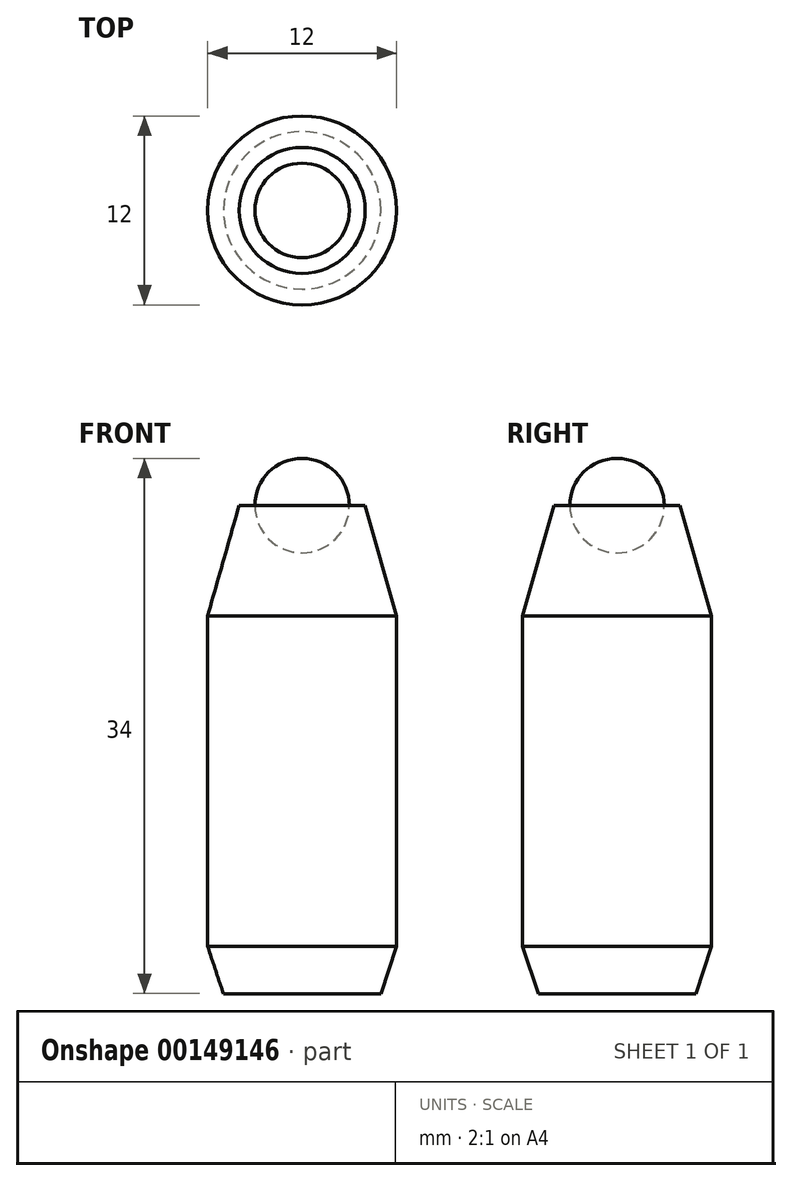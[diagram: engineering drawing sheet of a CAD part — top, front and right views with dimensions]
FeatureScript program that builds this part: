
annotation { "Feature Type Name" : "Feature", "Feature Type Description" : "" }
export const myFeature = defineFeature(function(context is Context, id is Id, definition is map)
    precondition{}
    {
        {
            var Q0;
            Q0=qCreatedBy(makeId("Front.planeOp"),FACE);
            var sketch = newSketch(context, id + "F0", { "sketchPlane" : qUnion([Q0])});
            skLineSegment(sketch, "E0", {"start": v(0, -13.95) * mm, "end": v(0, 17.05) * mm});
            skLineSegment(sketch, "E1", {"start": v(0, 17.05) * mm, "end": v(4, 17.05) * mm});
            skLineSegment(sketch, "E2", {"start": v(4, 17.05) * mm, "end": v(6, 10.05) * mm});
            skLineSegment(sketch, "E3", {"start": v(6, 10.05) * mm, "end": v(6, -10.95) * mm});
            skLineSegment(sketch, "E4", {"start": v(6, -10.95) * mm, "end": v(5, -13.95) * mm});
            skLineSegment(sketch, "E5", {"start": v(5, -13.95) * mm, "end": v(0, -13.95) * mm});
            skSolve(sketch);
        }
        {
            var Q0;
            Q0=makeQuery(id+"F0.imprint","IMPRINT",FACE,{"disambiguationData":[TD([[makeQuery(id+"F0.imprint","IMPRINT",EDGE,{"derivedFrom":sQuery(id+"F0.wireOp",EDGE,"E0")}),-1.0]])]});
            var Q1;
            Q1=sQuery(id+"F0.wireOp",EDGE,"E0");
            revolve(context, id + "F1", {"entities" : qUnion([Q0]), "axis" : qUnion([Q1]), "revolveType" : RevolveType.FULL});
        }
        {
            var Q0;
            Q0=makeQuery(id+"F1.opRevolve","SWEPT_FACE",FACE,{"disambiguationData":[OSD([sQuery(id+"F0.wireOp",EDGE,"E1")])]});
            var sketch = newSketch(context, id + "F2", { "sketchPlane" : qUnion([Q0])});
            skCircle(sketch, "E6", {"center": v(0, 0) * mm, "radius": 3 * mm});
            skLineSegment(sketch, "E7", {"start": v(-3, 0) * mm, "end": v(3, 0) * mm});
            skSolve(sketch);
        }
        {
            var Q0;
            {var subQ0=sQuery(id+"F2.wireOp",EDGE,"E7");Q0=makeQuery(id+"F2.imprint","IMPRINT",FACE,{"disambiguationData":[TD([[makeQuery(id+"F2.imprint","IMPRINT",EDGE,{"derivedFrom":subQ0}),1.0]])]});}
            var Q1;
            Q1=sQuery(id+"F2.wireOp",EDGE,"E7");
            revolve(context, id + "F3", {"entities" : qUnion([Q0]), "axis" : qUnion([Q1]), "revolveType" : RevolveType.FULL});
        }
    });
